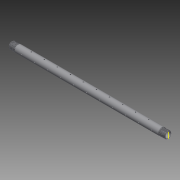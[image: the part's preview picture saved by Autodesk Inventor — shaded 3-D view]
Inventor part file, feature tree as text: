
AUTODESK INVENTOR PART (.ipt)
format: ipt  version: 2013 SP2 (Build 170200200, 200)  size: 1,251,840 bytes
history: native  units: in
note: dims shown in document units (in); Inventor stores cm internally (conversion verified against a paired STEP export)
features: sketch x3, other x2, plane x2, extrude x2, imported_body x1, projected_geometry x1
ambient origin geometry x8: Origin, YZ Plane, XZ Plane, XY Plane, X Axis, Y Axis, Z Axis, Center Point
feature tree (11):
  parser-record x1  (decoder bookkeeping rows leaked as tree rows — omitted from the tree; the rows remain in map.json)
  other  "4457K1141"
  plane  "Work Plane1"
  extrude  "Extrusion1"  Depth=0.125in
  plane  "Work Plane2"
  extrude  "Extrusion2"  Depth=3.937in
  sketch  "Sketch3"  dims[d10=1.0in d11=0.0in d12=0.42in d13=0.125in d14=0.7185in d15=4.3307in d17=1.5in d18=0.3937in d20=1.0in d22=1.0in d23=0.0in]
  imported_body  "Base1"
  sketch  "Sketch1"  dims[d0=0.42in d1=0.125in]
  projected_geometry  "Projected Loop1"
  sketch  "Sketch2"  dims[d2=1.4685in d3=3.937in d5=1.5in d6=0.3937in d8=1.0in]
